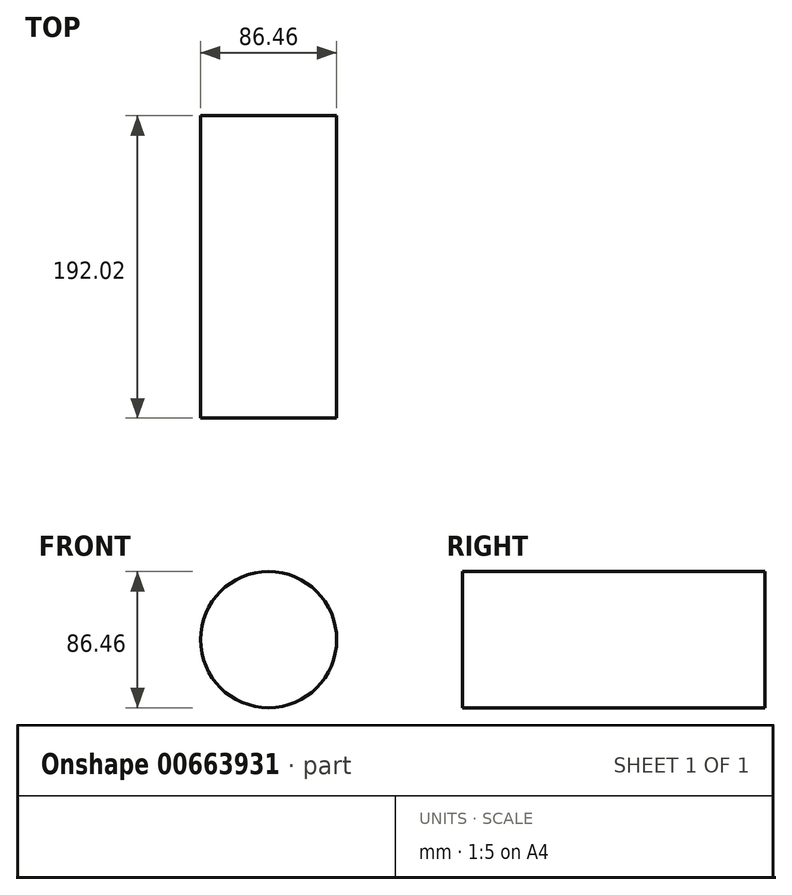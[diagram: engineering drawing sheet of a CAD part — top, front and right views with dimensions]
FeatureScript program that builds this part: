
annotation { "Feature Type Name" : "Feature", "Feature Type Description" : "" }
export const myFeature = defineFeature(function(context is Context, id is Id, definition is map)
    precondition{}
    {
        {
            var Q0;
            Q0=qCreatedBy(makeId("Front.planeOp"),FACE);
            var sketch = newSketch(context, id + "F0", { "sketchPlane" : qUnion([Q0])});
            skCircle(sketch, "E0", {"center": v(-114.9, 43.48) * mm, "radius": 43.23 * mm});
            skSolve(sketch);
        }
        {
            var Q0;
            Q0 = qSketchRegion(id + "F0", true);
            extrude(context, id + "F1", {"entities" : qUnion([Q0]), "depth" : 192.02 * mm, "offsetDistance" : 25.4 * mm});
        }
    });
